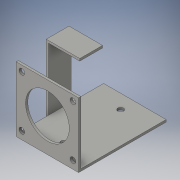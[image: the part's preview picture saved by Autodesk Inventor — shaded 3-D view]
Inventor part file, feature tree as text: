
AUTODESK INVENTOR PART (.ipt)
format: ipt  version: 2016 (Build 200138000, 138)  size: 179,200 bytes
history: native  units: in
note: dims shown in document units (in); Inventor stores cm internally (conversion verified against a paired STEP export)
features: extrude x5, sketch x5
ambient origin geometry x8: Origin, YZ Plane, XZ Plane, XY Plane, X Axis, Y Axis, Z Axis, Center Point
bodies: Solid1 (feature_tree)
feature tree (10):
  extrude  "Extrusion1"  Depth=2.1654in
  extrude  "Extrusion2"  Depth=1.0827in
  extrude  "Extrusion3"  Depth=0.1969in
  extrude  "Extrusion4"  Depth=0.1969in
  extrude  "Extrusion5"  Depth=0.0787in
  sketch  "Sketch1"  dims[d1=2.1654in d2=2.1654in]
  sketch  "Sketch2"  dims[d3=1.0827in d4=1.0827in]
  sketch  "Sketch3"  dims[d5=1.5157in d6=0.1969in]
  sketch  "Sketch4"  dims[d7=0.1969in d8=0.1969in]
  sketch  "Sketch5"  dims[d9=0.1969in d10=0.1969in d11=0.1969in d12=0.1969in d13=0.1969in d14=0.1969in d15=0.1969in d16=0.1969in d17=0.1969in d18=0.0787in d19=0.0in d20=2.9528in d21=0.0787in d22=3.0315in d23=2.1654in d24=0.0in d25=2.2441in d26=0.3937in d27=2.2441in d28=0.7874in d29=2.2441in d30=0.0787in d31=0.0in d32=1.1614in d33=0.7874in d34=0.0787in d35=0.0in d36=1.0827in d37=0.9843in d38=0.9843in d39=0.1969in d40=0.1969in d41=0.0787in d42=0.0in]
